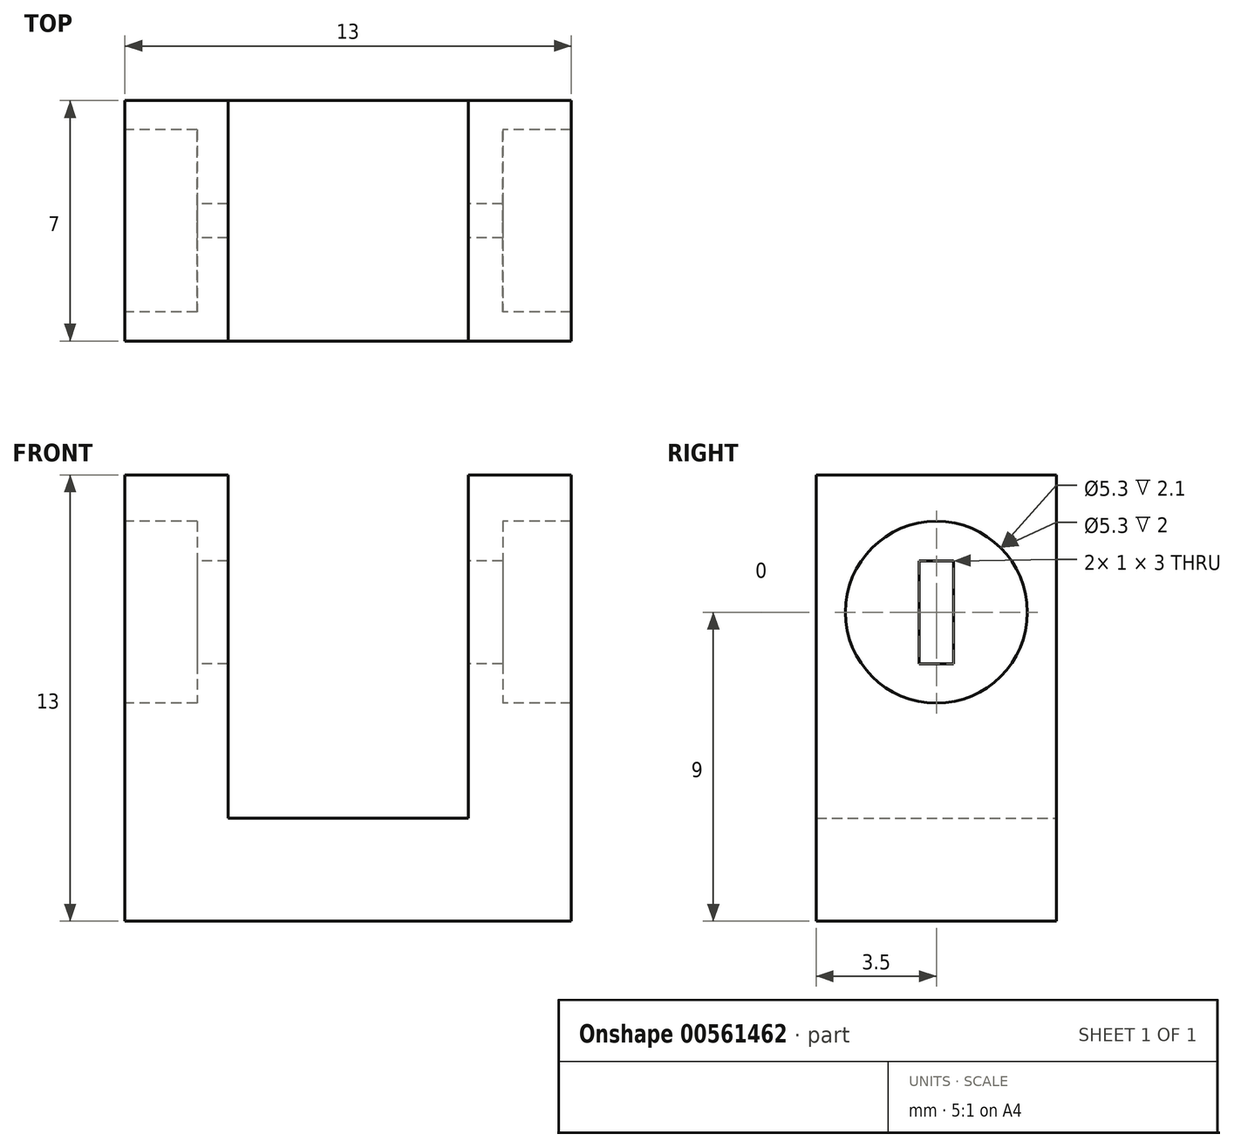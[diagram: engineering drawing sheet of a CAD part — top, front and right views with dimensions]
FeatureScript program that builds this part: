
annotation { "Feature Type Name" : "Feature", "Feature Type Description" : "" }
export const myFeature = defineFeature(function(context is Context, id is Id, definition is map)
    precondition{}
    {
        {
            var Q0;
            Q0=qCreatedBy(makeId("Front.planeOp"),FACE);
            var sketch = newSketch(context, id + "F0", { "sketchPlane" : qUnion([Q0])});
            skLineSegment(sketch, "E0.bottom", {"start": v(-6.56, 0) * mm, "end": v(-3.56, 0) * mm});
            skLineSegment(sketch, "E0.top", {"start": v(-6.56, 10) * mm, "end": v(-3.56, 10) * mm});
            skLineSegment(sketch, "E0.left", {"start": v(-6.56, 0) * mm, "end": v(-6.56, 10) * mm});
            skLineSegment(sketch, "E0.right", {"start": v(-3.56, 0) * mm, "end": v(-3.56, 10) * mm});
            skLineSegment(sketch, "E1.bottom", {"start": v(3.44, 0) * mm, "end": v(6.44, 0) * mm});
            skLineSegment(sketch, "E1.top", {"start": v(3.44, 10) * mm, "end": v(6.44, 10) * mm});
            skLineSegment(sketch, "E1.left", {"start": v(3.44, 0) * mm, "end": v(3.44, 10) * mm});
            skLineSegment(sketch, "E1.right", {"start": v(6.44, 0) * mm, "end": v(6.44, 10) * mm});
            skLineSegment(sketch, "E2.bottom", {"start": v(-6.56, 0) * mm, "end": v(6.44, 0) * mm});
            skLineSegment(sketch, "E2.top", {"start": v(-6.56, -3) * mm, "end": v(6.44, -3) * mm});
            skLineSegment(sketch, "E2.left", {"start": v(-6.56, 0) * mm, "end": v(-6.56, -3) * mm});
            skLineSegment(sketch, "E2.right", {"start": v(6.44, 0) * mm, "end": v(6.44, -3) * mm});
            skSolve(sketch);
        }
        {
            var Q0;
            Q0=makeQuery(id+"F0.imprint","IMPRINT",FACE,{"disambiguationData":[TD([[makeQuery(id+"F0.imprint","IMPRINT",EDGE,{"derivedFrom":sQuery(id+"F0.wireOp",EDGE,"E0.top")}),-1.0]])]});
            var Q1;
            Q1=makeQuery(id+"F0.imprint","IMPRINT",FACE,{"disambiguationData":[TD([[makeQuery(id+"F0.imprint","IMPRINT",EDGE,{"derivedFrom":sQuery(id+"F0.wireOp",EDGE,"E2.top")}),1.0]])]});
            var Q2;
            Q2=makeQuery(id+"F0.imprint","IMPRINT",FACE,{"disambiguationData":[TD([[makeQuery(id+"F0.imprint","IMPRINT",EDGE,{"derivedFrom":sQuery(id+"F0.wireOp",EDGE,"E1.top")}),-1.0]])]});
            extrude(context, id + "F1", {"entities" : qUnion([Q0, Q1, Q2]), "depth" : 7 * mm, "offsetDistance" : 25 * mm, "symmetric" : true});
        }
        {
            var Q0;
            Q0=makeQuery(id+"F1.opExtrude","SWEPT_FACE",FACE,{"disambiguationData":[OSD([sQuery(id+"F0.wireOp",EDGE,"E0.left"),sQuery(id+"F0.wireOp",EDGE,"E2.left")])]});
            var sketch = newSketch(context, id + "F2", { "sketchPlane" : qUnion([Q0])});
            skCircle(sketch, "E3", {"center": v(0, 6) * mm, "radius": 2.65 * mm});
            skLineSegment(sketch, "E4.bottom", {"start": v(-0.5, 7.5) * mm, "end": v(0.5, 7.5) * mm});
            skLineSegment(sketch, "E4.top", {"start": v(-0.5, 4.5) * mm, "end": v(0.5, 4.5) * mm});
            skLineSegment(sketch, "E4.left", {"start": v(-0.5, 8.6) * mm, "end": v(-0.5, 3.4) * mm});
            skLineSegment(sketch, "E4.right", {"start": v(0.5, 8.6) * mm, "end": v(0.5, 3.4) * mm});
            skSolve(sketch);
        }
        {
            var Q0;
            {var subQ0=sQuery(id+"F2.wireOp",EDGE,"E4.bottom");Q0=makeQuery(id+"F2.imprint","IMPRINT",FACE,{"disambiguationData":[TD([[makeQuery(id+"F2.imprint","IMPRINT",EDGE,{"derivedFrom":subQ0}),-1.0]])]});}
            extrude(context, id + "F3", {"entities" : qUnion([Q0]), "operationType" : NewBodyOperationType.REMOVE, "oppositeDirection" : true, "depth" : 50 * mm, "offsetDistance" : 25 * mm, "symmetric" : true});
        }
        {
            var Q0;
            {var subQ0=sQuery(id+"F2.wireOp",EDGE,"E4.left");var subQ1=sQuery(id+"F2.wireOp",EDGE,"E3");var subQ2=makeQuery(id+"F2.imprint","INTERSECT",VERTEX,{"disambiguationData":[OD(0.0)],"derivedFrom":[subQ1,subQ0]});Q0=makeQuery(id+"F2.imprint","IMPRINT",FACE,{"disambiguationData":[TD([[makeQuery(id+"F2.imprint","IMPRINT",EDGE,{"disambiguationData":[TD([[subQ2,-1.0]])],"derivedFrom":subQ1}),1.0]])]});}
            var Q1;
            {var subQ0=sQuery(id+"F2.wireOp",EDGE,"E4.right");var subQ1=sQuery(id+"F2.wireOp",EDGE,"E3");var subQ2=makeQuery(id+"F2.imprint","INTERSECT",VERTEX,{"disambiguationData":[OD(0.0)],"derivedFrom":[subQ1,subQ0]});Q1=makeQuery(id+"F2.imprint","IMPRINT",FACE,{"disambiguationData":[TD([[makeQuery(id+"F2.imprint","IMPRINT",EDGE,{"disambiguationData":[TD([[subQ2,1.0]])],"derivedFrom":subQ1}),1.0]])]});}
            var Q2;
            {var subQ5=sQuery(id+"F2.wireOp",EDGE,"E4.bottom");Q2=makeQuery(id+"F2.imprint","IMPRINT",FACE,{"disambiguationData":[TD([[makeQuery(id+"F2.imprint","IMPRINT",EDGE,{"derivedFrom":subQ5}),1.0]])]});}
            var Q3;
            {var subQ5=sQuery(id+"F2.wireOp",EDGE,"E4.top");Q3=makeQuery(id+"F2.imprint","IMPRINT",FACE,{"disambiguationData":[TD([[makeQuery(id+"F2.imprint","IMPRINT",EDGE,{"derivedFrom":subQ5}),-1.0]])]});}
            extrude(context, id + "F4", {"entities" : qUnion([Q0, Q1, Q2, Q3]), "operationType" : NewBodyOperationType.REMOVE, "oppositeDirection" : true, "depth" : 2.1 * mm, "offsetDistance" : 25 * mm});
        }
        {
            var Q0;
            {var subQ0=sQuery(id+"F2.wireOp",EDGE,"E4.left");var subQ1=sQuery(id+"F2.wireOp",EDGE,"E3");var subQ2=makeQuery(id+"F2.imprint","INTERSECT",VERTEX,{"disambiguationData":[OD(0.0)],"derivedFrom":[subQ1,subQ0]});Q0=makeQuery(id+"F2.imprint","IMPRINT",FACE,{"disambiguationData":[TD([[makeQuery(id+"F2.imprint","IMPRINT",EDGE,{"disambiguationData":[TD([[subQ2,-1.0]])],"derivedFrom":subQ1}),1.0]])]});}
            var Q1;
            {var subQ5=sQuery(id+"F2.wireOp",EDGE,"E4.bottom");Q1=makeQuery(id+"F2.imprint","IMPRINT",FACE,{"disambiguationData":[TD([[makeQuery(id+"F2.imprint","IMPRINT",EDGE,{"derivedFrom":subQ5}),1.0]])]});}
            var Q2;
            {var subQ5=sQuery(id+"F2.wireOp",EDGE,"E4.top");Q2=makeQuery(id+"F2.imprint","IMPRINT",FACE,{"disambiguationData":[TD([[makeQuery(id+"F2.imprint","IMPRINT",EDGE,{"derivedFrom":subQ5}),-1.0]])]});}
            var Q3;
            {var subQ0=sQuery(id+"F2.wireOp",EDGE,"E4.right");var subQ1=sQuery(id+"F2.wireOp",EDGE,"E3");var subQ2=makeQuery(id+"F2.imprint","INTERSECT",VERTEX,{"disambiguationData":[OD(0.0)],"derivedFrom":[subQ1,subQ0]});Q3=makeQuery(id+"F2.imprint","IMPRINT",FACE,{"disambiguationData":[TD([[makeQuery(id+"F2.imprint","IMPRINT",EDGE,{"disambiguationData":[TD([[subQ2,1.0]])],"derivedFrom":subQ1}),1.0]])]});}
            extrude(context, id + "F5", {"entities" : qUnion([Q0, Q1, Q2, Q3]), "operationType" : NewBodyOperationType.REMOVE, "oppositeDirection" : true, "depth" : 15 * mm, "offsetDistance" : 25 * mm, "hasSecondDirection" : true, "secondDirectionOppositeDirection" : true, "secondDirectionDepth" : 11 * mm});
        }
    });
